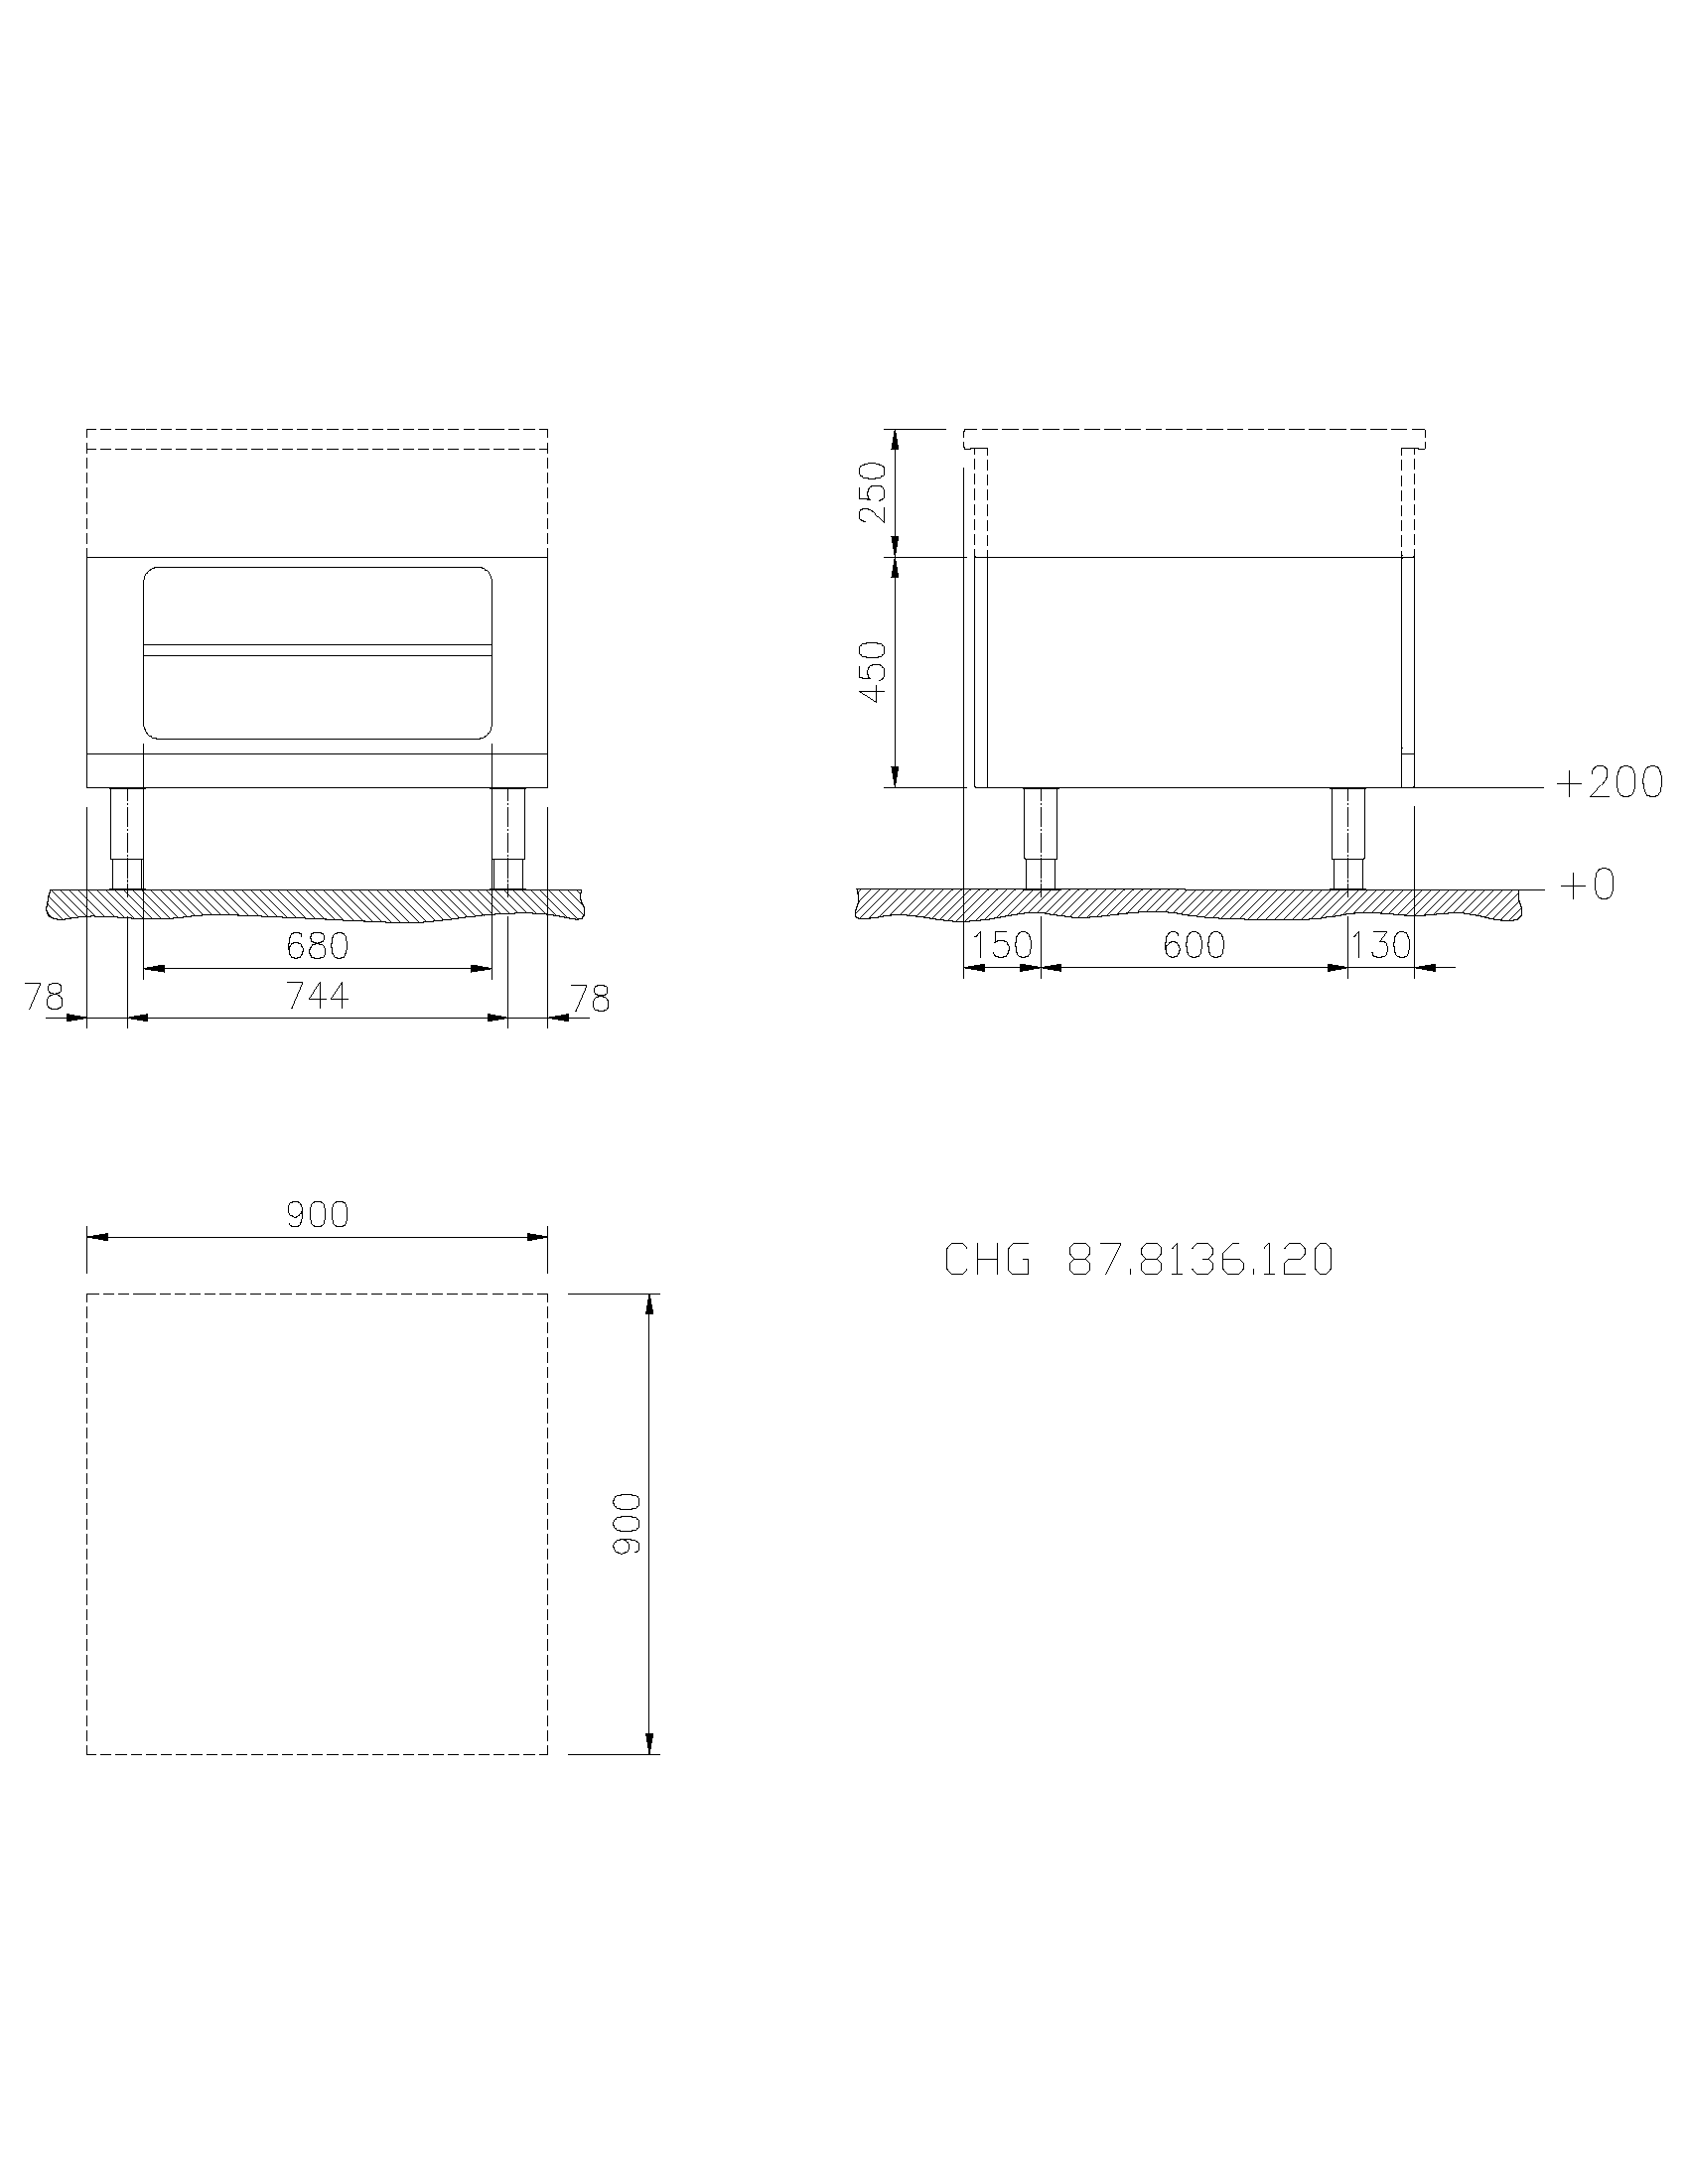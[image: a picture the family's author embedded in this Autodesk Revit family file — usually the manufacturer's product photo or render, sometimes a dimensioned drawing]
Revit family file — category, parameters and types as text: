
# Revit family: QF_ELECTROLUXPROFESSIONAL_593339_MCKDEBDDVO
name_source: partatom
category: Specialty Equipment
units: mm (PartAtom-declared; Revit-internal decimal feet)

## family parameters
Always vertical = Yes
Cut with Voids When Loaded = No
Enable Cutting in Views = No
Maintain Annotation Orientation = No
Part Type = Normal
Room Calculation Point = No
Round Connector Dimension = Use Diameter
Shared = No
Work Plane-Based = No

## types (1)
- Standard
    Accessory = No
    Cold Water Size = 1"
    Compressed Air Pressure = 0.00 psi
    Compressed Air Size = 0"
    Compressed Air Volume = 0 GPM
    Condensate Return Size = 0"
    Cycle = 50 Hz
    Default Elevation = 0 mm  [stored 0 ft]
    Depth Actual = 900 mm  [stored 2.95276 ft]
    Description = GAS PASTA COOKER, TOWNGAS, 24,5L, 1-SIDE, BSPL, 400X900X700H
    Direct Waste Size = 1"
    Gas Input Pressure = 2.5
    Gas KW = 9.5
    Gas Size = 1"
    HP = 0 HP
    Height Actual = 700 mm  [stored 2.29659 ft]
    Hot Water Size = 0"
    Item Number = 593339
    Length Actual = 400 mm  [stored 1.31234 ft]
    Manufacturer = Electrolux Professional
    Model = MCKDEBDDVO
    Phase = 3
    Refrigerant Compressor Remote = Yes
    Refrigeration Liquid Line Size = 0 mm  [stored 0 ft]
    Refrigeration Suction Line Size = 0 mm  [stored 0 ft]
    Steam Consumption per Hour = 0
    Steam Supply Maximum Pressure = 0.00 psi
    Steam Supply Minimum Pressure = 0.00 psi
    Steam Supply Size = 0"
    URL = http://www.electroluxprofessional.com
    URL Manufacturer = http://www.electroluxprofessional.com
    Volts = 440 V
    Watts = 0 W
    Weight = 73.00 kg

note: source unit labels omitted for Gas Input Pressure — the stored unit's dimension contradicts the parameter name (converter mislabeling)

note: [stored X ft] marks values corroborated as IEEE doubles in the binary element streams (Revit-internal decimal feet)

## geometry (parser evidence)
native form markers: Blend x4, Sweep x11
no freeform markers — native parametric forms only
